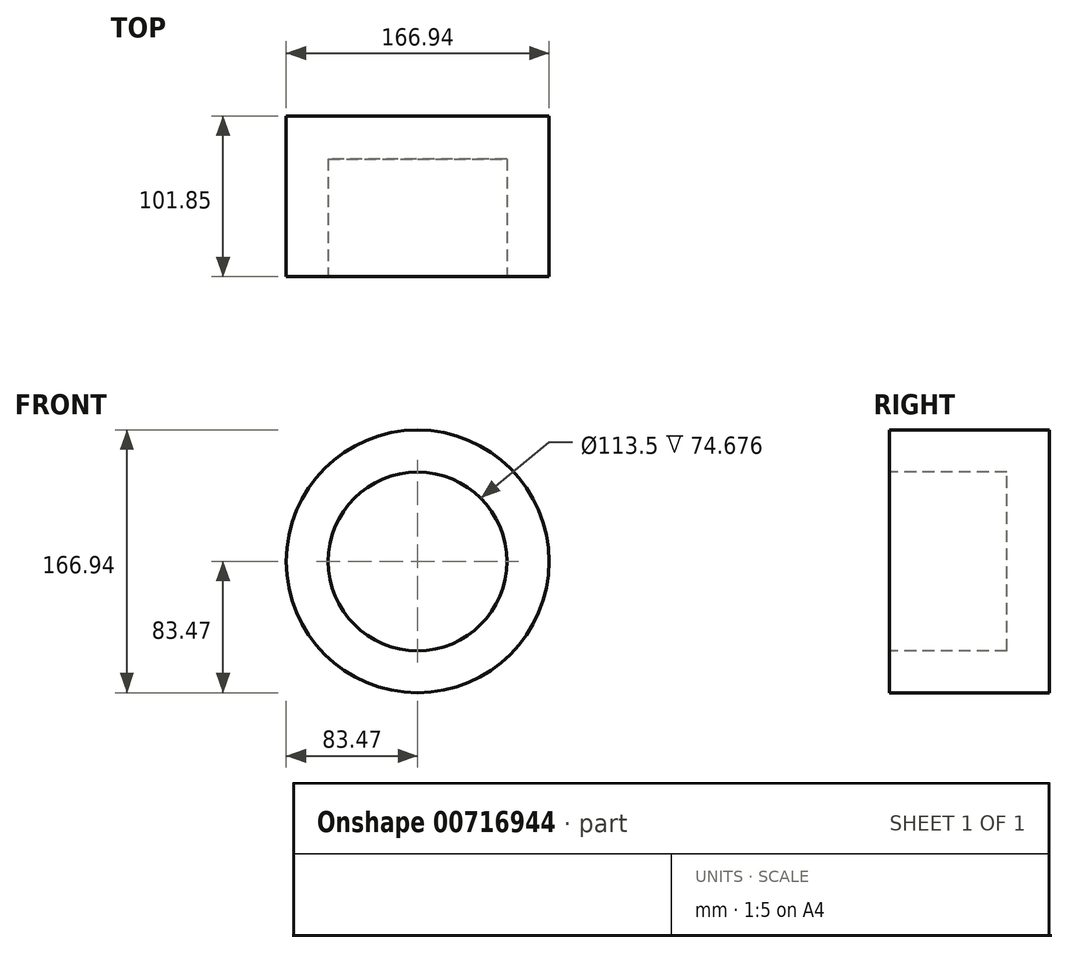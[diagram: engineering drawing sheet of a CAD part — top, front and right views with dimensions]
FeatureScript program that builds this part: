
annotation { "Feature Type Name" : "Feature", "Feature Type Description" : "" }
export const myFeature = defineFeature(function(context is Context, id is Id, definition is map)
    precondition{}
    {
        {
            var Q0;
            Q0=qCreatedBy(makeId("Front.planeOp"),FACE);
            var sketch = newSketch(context, id + "F0", { "sketchPlane" : qUnion([Q0])});
            skCircle(sketch, "E0", {"center": v(0, 0) * mm, "radius": 83.47 * mm});
            skSolve(sketch);
        }
        {
            var Q0;
            Q0=qSketchRegion(id+"F0",true);
            extrude(context, id + "F1", {"entities" : qUnion([Q0]), "depth" : 101.85 * mm, "offsetDistance" : 25.4 * mm});
        }
        {
            var Q0;
            Q0=makeQuery(id+"F1.opExtrude","CAP_FACE",FACE,{"disambiguationData":[OSD([sQuery(id+"F0.wireOp",EDGE,"E0")])],"isStart":false});
            var sketch = newSketch(context, id + "F2", { "sketchPlane" : qUnion([Q0])});
            skCircle(sketch, "E1", {"center": v(0, 0) * mm, "radius": 56.75 * mm});
            skSolve(sketch);
        }
        {
            var Q0;
            Q0=makeQuery(id+"F2.imprint","IMPRINT",FACE,{"disambiguationData":[TD([[makeQuery(id+"F2.imprint","IMPRINT",EDGE,{"derivedFrom":sQuery(id+"F2.wireOp",EDGE,"E1")}),1.0]])]});
            extrude(context, id + "F3", {"entities" : qUnion([Q0]), "operationType" : NewBodyOperationType.REMOVE, "oppositeDirection" : true, "depth" : 74.68 * mm, "offsetDistance" : 25.4 * mm});
        }
    });
